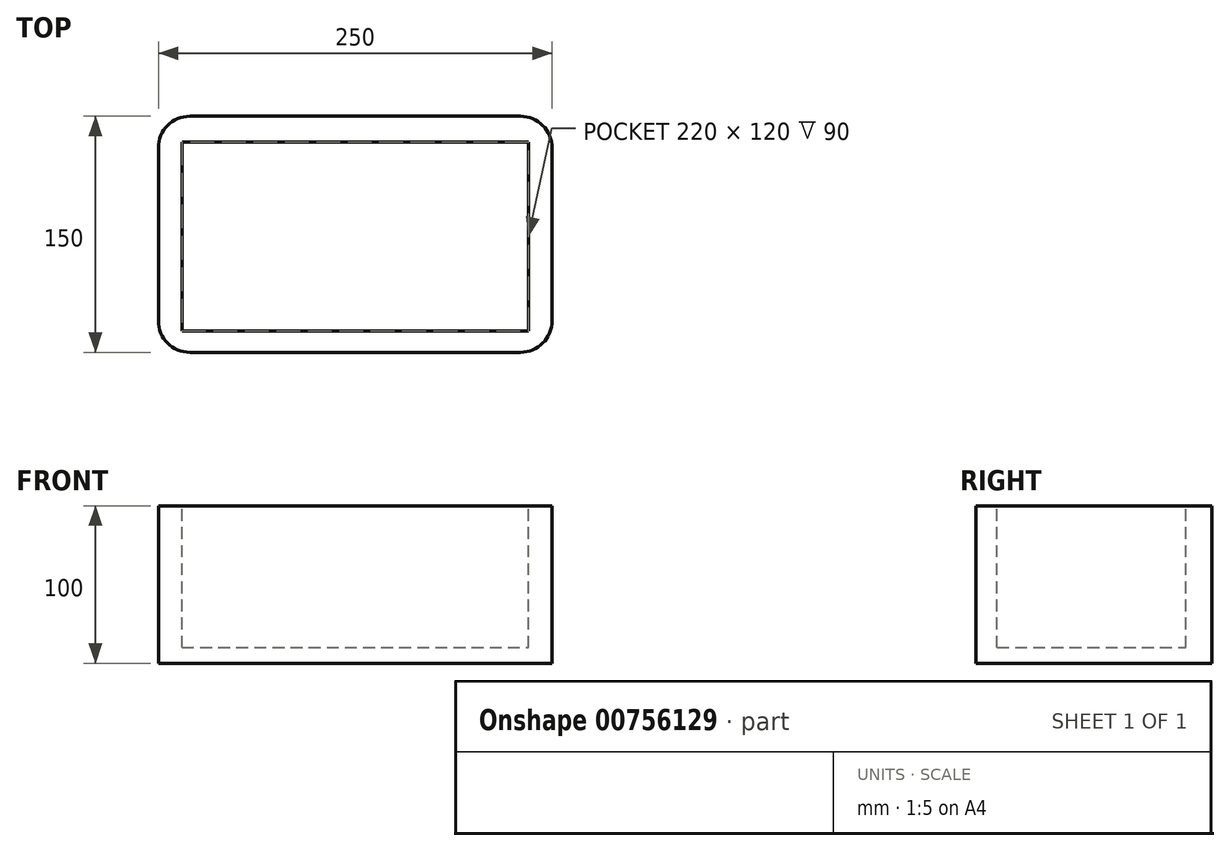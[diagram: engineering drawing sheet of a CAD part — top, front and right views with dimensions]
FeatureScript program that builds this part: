
annotation { "Feature Type Name" : "Feature", "Feature Type Description" : "" }
export const myFeature = defineFeature(function(context is Context, id is Id, definition is map)
    precondition{}
    {
        {
            var Q0;
            Q0=qCreatedBy(makeId("Top.planeOp"),FACE);
            var sketch = newSketch(context, id + "F0", { "sketchPlane" : qUnion([Q0])});
            skLineSegment(sketch, "E0.bottom", {"start": v(-125, -75) * mm, "end": v(125, -75) * mm});
            skLineSegment(sketch, "E0.top", {"start": v(-125, 75) * mm, "end": v(125, 75) * mm});
            skLineSegment(sketch, "E0.left", {"start": v(-125, -75) * mm, "end": v(-125, 75) * mm});
            skLineSegment(sketch, "E0.right", {"start": v(125, -75) * mm, "end": v(125, 75) * mm});
            skPoint(sketch, "E0.middle", {"position": v(0, 0) * mm});
            skSolve(sketch);
        }
        {
            var Q0;
            Q0=makeQuery(id+"F0.imprint","IMPRINT",FACE,{"disambiguationData":[TD([[makeQuery(id+"F0.imprint","IMPRINT",EDGE,{"derivedFrom":sQuery(id+"F0.wireOp",EDGE,"E0.bottom")}),1.0]])]});
            extrude(context, id + "F1", {"entities" : qUnion([Q0]), "depth" : 100 * mm, "offsetDistance" : 25 * mm});
        }
        {
            var Q0;
            Q0=makeQuery(id+"F1.opExtrude","CAP_FACE",FACE,{"disambiguationData":[OSD([sQuery(id+"F0.wireOp",EDGE,"E0.bottom"),sQuery(id+"F0.wireOp",EDGE,"E0.top"),sQuery(id+"F0.wireOp",EDGE,"E0.left"),sQuery(id+"F0.wireOp",EDGE,"E0.right")])],"isStart":false});
            var sketch = newSketch(context, id + "F2", { "sketchPlane" : qUnion([Q0])});
            skLineSegment(sketch, "E1.bottom", {"start": v(-110, -61.49) * mm, "end": v(110, -61.49) * mm});
            skLineSegment(sketch, "E1.top", {"start": v(-110, 58.51) * mm, "end": v(110, 58.51) * mm});
            skLineSegment(sketch, "E1.left", {"start": v(-110, -61.49) * mm, "end": v(-110, 58.51) * mm});
            skLineSegment(sketch, "E1.right", {"start": v(110, -61.49) * mm, "end": v(110, 58.51) * mm});
            skPoint(sketch, "E1.middle", {"position": v(0, -1.49) * mm});
            skSolve(sketch);
        }
        {
            var Q0;
            Q0=makeQuery(id+"F2.imprint","IMPRINT",FACE,{"disambiguationData":[TD([[makeQuery(id+"F2.imprint","IMPRINT",EDGE,{"derivedFrom":sQuery(id+"F2.wireOp",EDGE,"E1.bottom")}),1.0]])]});
            extrude(context, id + "F3", {"entities" : qUnion([Q0]), "operationType" : NewBodyOperationType.REMOVE, "oppositeDirection" : true, "depth" : 90 * mm, "offsetDistance" : 25 * mm});
        }
        {
            var Q0;
            Q0=makeQuery(id+"F1.opExtrude","SWEPT_EDGE",EDGE,{"disambiguationData":[OSD([sQuery(id+"F0.wireOp",EDGE,"E0.bottom"),sQuery(id+"F0.wireOp",EDGE,"E0.right")])]});
            var Q1;
            Q1=makeQuery(id+"F1.opExtrude","SWEPT_EDGE",EDGE,{"disambiguationData":[OSD([sQuery(id+"F0.wireOp",EDGE,"E0.top"),sQuery(id+"F0.wireOp",EDGE,"E0.right")])]});
            var Q2;
            Q2=makeQuery(id+"F1.opExtrude","SWEPT_EDGE",EDGE,{"disambiguationData":[OSD([sQuery(id+"F0.wireOp",EDGE,"E0.top"),sQuery(id+"F0.wireOp",EDGE,"E0.left")])]});
            var Q3;
            Q3=makeQuery(id+"F1.opExtrude","SWEPT_EDGE",EDGE,{"disambiguationData":[OSD([sQuery(id+"F0.wireOp",EDGE,"E0.bottom"),sQuery(id+"F0.wireOp",EDGE,"E0.left")])]});
            fillet(context, id + "F4", {"entities" : qUnion([Q0, Q1, Q2, Q3]), "tangentPropagation" : true, "radius" : 20 * mm, "defaultsChanged" : false, "vertexSettings" : [], "allowEdgeOverflow" : false});
        }
    });
